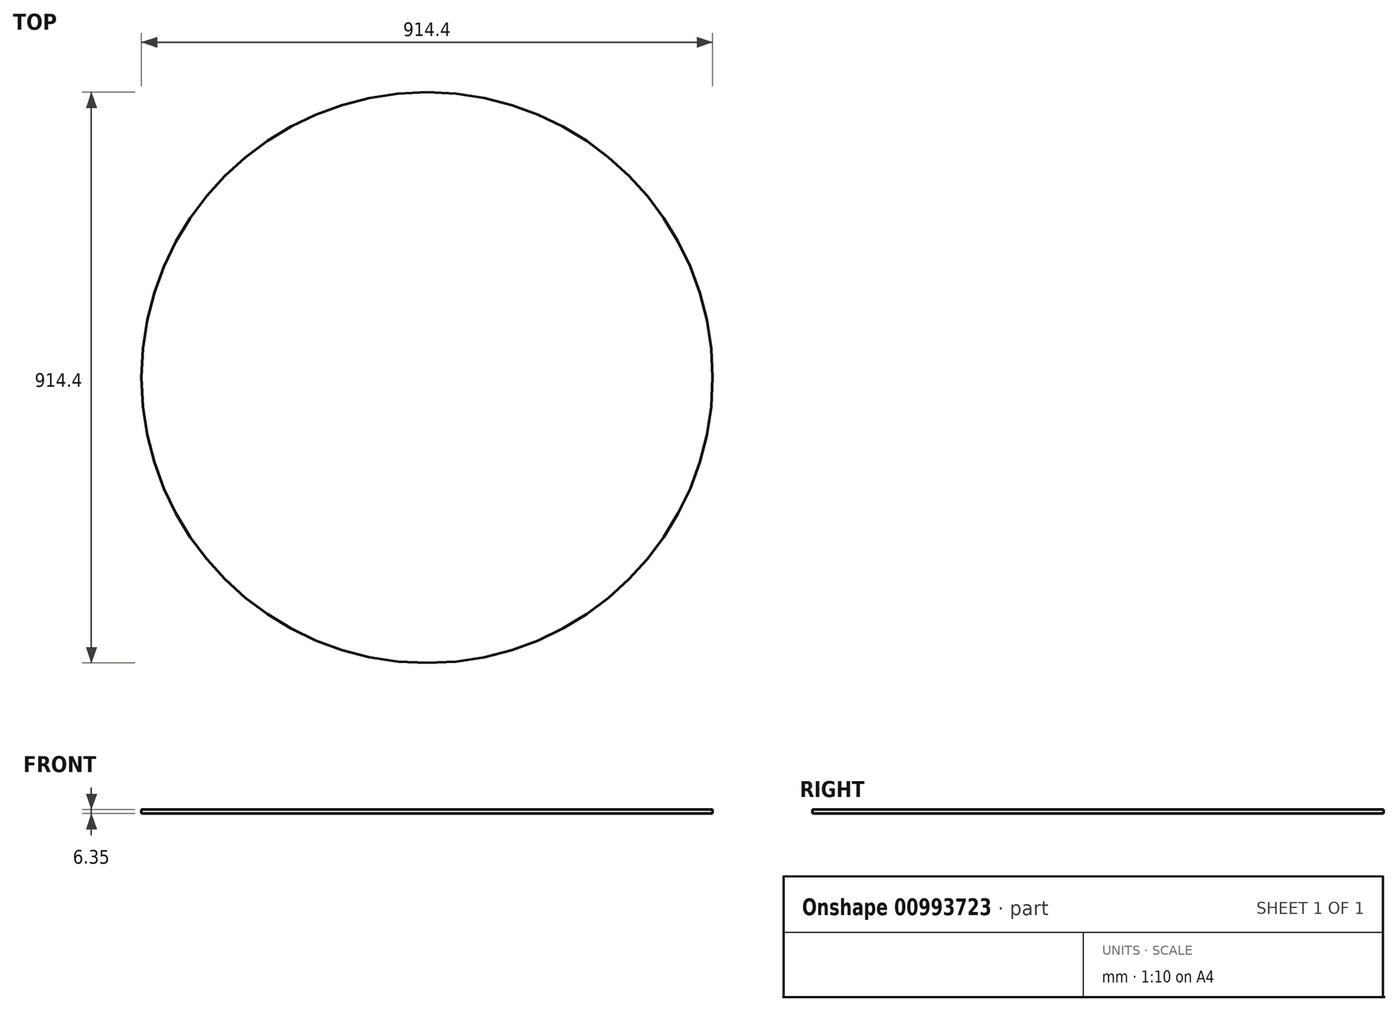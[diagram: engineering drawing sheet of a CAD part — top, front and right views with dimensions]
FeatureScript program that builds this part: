
annotation { "Feature Type Name" : "Feature", "Feature Type Description" : "" }
export const myFeature = defineFeature(function(context is Context, id is Id, definition is map)
    precondition{}
    {
        {
            var Q0;
            Q0=qCreatedBy(makeId("Top.planeOp"),FACE);
            var sketch = newSketch(context, id + "F0", { "sketchPlane" : qUnion([Q0])});
            skCircle(sketch, "E0", {"center": v(0, 0) * mm, "radius": 457.2 * mm});
            skSolve(sketch);
        }
        {
            var Q0;
            Q0 = qSketchRegion(id + "F0", true);
            extrude(context, id + "F1", {"entities" : qUnion([Q0]), "depth" : 6.35 * mm, "offsetDistance" : 25.4 * mm});
        }
    });
